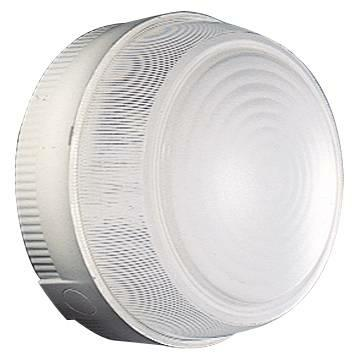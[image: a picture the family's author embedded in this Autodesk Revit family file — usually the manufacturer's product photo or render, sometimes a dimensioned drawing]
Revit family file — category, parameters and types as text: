
# Revit family: Lighting-Terziario-GEWISS-TONDAES-PLAFONIERE_180
name_source: partatom
category: Apparecchi per illuminazione
units: mm (PartAtom-declared; Revit-internal decimal feet)

## family parameters
Condiviso = No
Host = Superficie
Numero OmniClass = 23.80.70.00
Punto di calcolo locali = Sì
Quota connettore circolare = Usa diametro
Sorgente d'illuminazione = Sì
Taglio con vuoti quando caricato = No
Tipo di parte = Normale
Titolo OmniClass = Lighting

## types (1)
- GW80651 - Per lampada E27 60W - Grigio RAL 7035 - IP44
    Angolo inclinazione = 0.00°
    Applicazione = Interno / Esterno
    Attacco lampada = E27
    Carico apparente = 60 VA
    Catalogo = LIGHTING
    Catalogo Serie = TONDA ES
    Classe di efficienza lampada fornita = D ÷ A+
    Classe di efficienza lampade compatibili = D ÷ A+
    Classe isolamento = II
    Codice EAN = 8011564068773
    Codice Electrocod = 2415
    Colore = Grigio RAL 7035
    Commenti sul wattaggio = 60W
    Descrizione = TONDA ES 180 60W E27 IP44 RAL7035
    File diagramma fotometrico = GW80651-80651387.IES
    Filtro dei colori = 16777215
    Glow Wire Test = 850°C
    Grado di protezione = IP44
    IDF = 66a3af5a-cce8-4cc5-a8e0-fb64ecd5527a
    IDT = 1579acc9-57b9-4df1-98d5-0dac6674b181
    Immagine tipo = GW80651.jpg
    Lampada = E27
    Materiale = Policarbonato
    Modello = GW80651
    Numero di poli = 2
    Peso (kg) = 0,3
    Peso (kg): = 0,3
    Potenza lampada = 60W
    Potenza lampada max = 60W
    Produttore = GEWISS S.p.A.
    Prospetto di default = 1219 mm
    Resistenza agli urti = IK10
    SEO = Plafoniera
    Scheda Tecnica = https://www.gewiss.com
    URL = https://www.gewiss.com
    Variazione temperatura colore lampada con luminosità attenuata = <Nessuno>
    Versione file RFA = 20.11
    Voltaggio = 230 V
